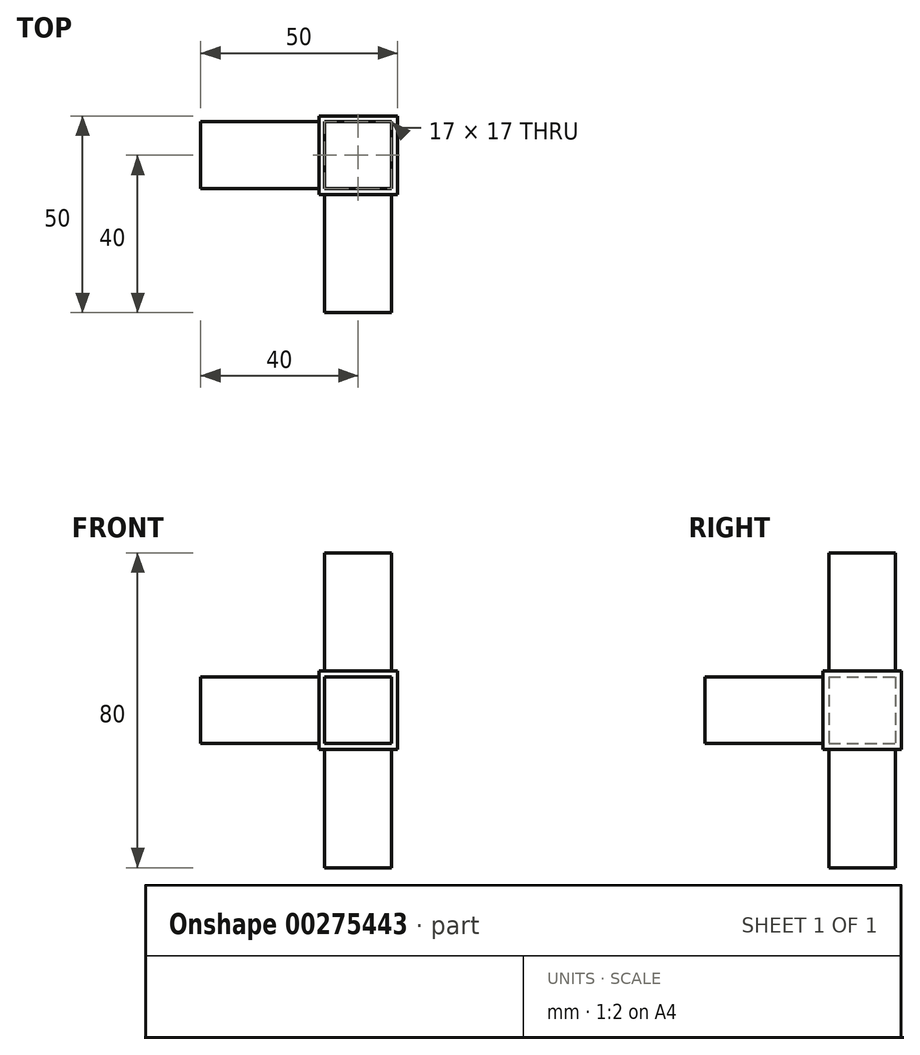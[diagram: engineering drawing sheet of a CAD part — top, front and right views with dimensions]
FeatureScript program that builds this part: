
annotation { "Feature Type Name" : "Feature", "Feature Type Description" : "" }
export const myFeature = defineFeature(function(context is Context, id is Id, definition is map)
    precondition{}
    {
        {
            var Q0;
            Q0=qCreatedBy(makeId("Top.planeOp"),FACE);
            var sketch = newSketch(context, id + "F0", { "sketchPlane" : qUnion([Q0])});
            skLineSegment(sketch, "E0.bottom", {"start": v(10, -10) * mm, "end": v(-10, -10) * mm});
            skLineSegment(sketch, "E0.top", {"start": v(10, 10) * mm, "end": v(-10, 10) * mm});
            skLineSegment(sketch, "E0.left", {"start": v(10, -10) * mm, "end": v(10, 10) * mm});
            skLineSegment(sketch, "E0.right", {"start": v(-10, -10) * mm, "end": v(-10, 10) * mm});
            skPoint(sketch, "E0.middle", {"position": v(0, 0) * mm});
            skLineSegment(sketch, "E1", {"start": v(0, -10) * mm, "end": v(8.5, -10) * mm});
            skLineSegment(sketch, "E2.bottom", {"start": v(8.5, -10) * mm, "end": v(-8.5, -10) * mm});
            skLineSegment(sketch, "E2.top", {"start": v(8.5, -40) * mm, "end": v(-8.5, -40) * mm});
            skLineSegment(sketch, "E2.left", {"start": v(8.5, -10) * mm, "end": v(8.5, -40) * mm});
            skLineSegment(sketch, "E2.right", {"start": v(-8.5, -10) * mm, "end": v(-8.5, -40) * mm});
            skLineSegment(sketch, "E3", {"start": v(-10, 0) * mm, "end": v(-10, -8.5) * mm});
            skLineSegment(sketch, "E4.bottom", {"start": v(-10, -8.5) * mm, "end": v(-40, -8.5) * mm});
            skLineSegment(sketch, "E4.top", {"start": v(-10, 8.5) * mm, "end": v(-40, 8.5) * mm});
            skLineSegment(sketch, "E4.left", {"start": v(-10, -8.5) * mm, "end": v(-10, 8.5) * mm});
            skLineSegment(sketch, "E4.right", {"start": v(-40, -8.5) * mm, "end": v(-40, 8.5) * mm});
            skSolve(sketch);
        }
        {
            var Q0;
            {var subQ1=sQuery(id+"F0.wireOp",EDGE,"E0.top");Q0=makeQuery(id+"F0.imprint","IMPRINT",FACE,{"disambiguationData":[TD([[makeQuery(id+"F0.imprint","IMPRINT",EDGE,{"derivedFrom":subQ1}),1.0]])]});}
            extrude(context, id + "F1", {"entities" : qUnion([Q0]), "depth" : 20 * mm});
        }
        {
            var Q0;
            {var subQ4=sQuery(id+"F0.wireOp",EDGE,"E4.bottom");Q0=makeQuery(id+"F0.imprint","IMPRINT",FACE,{"disambiguationData":[TD([[makeQuery(id+"F0.imprint","IMPRINT",EDGE,{"derivedFrom":subQ4}),-1.0]])]});}
            var Q1;
            Q1=makeQuery(id+"F0.imprint","IMPRINT",FACE,{"disambiguationData":[TD([[makeQuery(id+"F0.imprint","IMPRINT",EDGE,{"derivedFrom":sQuery(id+"F0.wireOp",EDGE,"E2.top")}),-1.0]])]});
            extrude(context, id + "F2", {"entities" : qUnion([Q0, Q1]), "operationType" : NewBodyOperationType.ADD, "depth" : 18.5 * mm, "hasSecondDirection" : true, "secondDirectionOppositeDirection" : false, "secondDirectionDepth" : 1.5 * mm});
        }
        {
            var Q0;
            Q0=makeQuery(id+"F1.opExtrude","CAP_FACE",FACE,{"disambiguationData":[OSD([sQuery(id+"F0.wireOp",EDGE,"E0.bottom"),sQuery(id+"F0.wireOp",EDGE,"E0.top"),sQuery(id+"F0.wireOp",EDGE,"E0.left"),sQuery(id+"F0.wireOp",EDGE,"E0.right"),sQuery(id+"F0.wireOp",EDGE,"E2.bottom"),sQuery(id+"F0.wireOp",EDGE,"E4.left")])],"isStart":false});
            var sketch = newSketch(context, id + "F3", { "sketchPlane" : qUnion([Q0])});
            skLineSegment(sketch, "E5.bottom", {"start": v(8.5, -8.5) * mm, "end": v(-8.5, -8.5) * mm});
            skLineSegment(sketch, "E5.top", {"start": v(8.5, 8.5) * mm, "end": v(-8.5, 8.5) * mm});
            skLineSegment(sketch, "E5.left", {"start": v(8.5, -8.5) * mm, "end": v(8.5, 8.5) * mm});
            skLineSegment(sketch, "E5.right", {"start": v(-8.5, -8.5) * mm, "end": v(-8.5, 8.5) * mm});
            skPoint(sketch, "E5.middle", {"position": v(0, 0) * mm});
            skSolve(sketch);
        }
        {
            var Q0;
            Q0=qSketchRegion(id+"F3",true);
            extrude(context, id + "F4", {"entities" : qUnion([Q0]), "operationType" : NewBodyOperationType.ADD, "depth" : 30 * mm});
        }
        {
            var Q0;
            Q0=makeQuery(id+"F1.opExtrude","CAP_FACE",FACE,{"disambiguationData":[OSD([sQuery(id+"F0.wireOp",EDGE,"E0.bottom"),sQuery(id+"F0.wireOp",EDGE,"E0.top"),sQuery(id+"F0.wireOp",EDGE,"E0.left"),sQuery(id+"F0.wireOp",EDGE,"E0.right"),sQuery(id+"F0.wireOp",EDGE,"E2.bottom"),sQuery(id+"F0.wireOp",EDGE,"E4.left")])],"isStart":true});
            var sketch = newSketch(context, id + "F5", { "sketchPlane" : qUnion([Q0])});
            skLineSegment(sketch, "E6.bottom", {"start": v(8.5, -8.5) * mm, "end": v(-8.5, -8.5) * mm});
            skLineSegment(sketch, "E6.top", {"start": v(8.5, 8.5) * mm, "end": v(-8.5, 8.5) * mm});
            skLineSegment(sketch, "E6.left", {"start": v(8.5, -8.5) * mm, "end": v(8.5, 8.5) * mm});
            skLineSegment(sketch, "E6.right", {"start": v(-8.5, -8.5) * mm, "end": v(-8.5, 8.5) * mm});
            skPoint(sketch, "E6.middle", {"position": v(0, 0) * mm});
            skSolve(sketch);
        }
        {
            var Q0;
            Q0=qSketchRegion(id+"F5",true);
            extrude(context, id + "F6", {"entities" : qUnion([Q0]), "operationType" : NewBodyOperationType.ADD, "depth" : 30 * mm});
        }
    });
